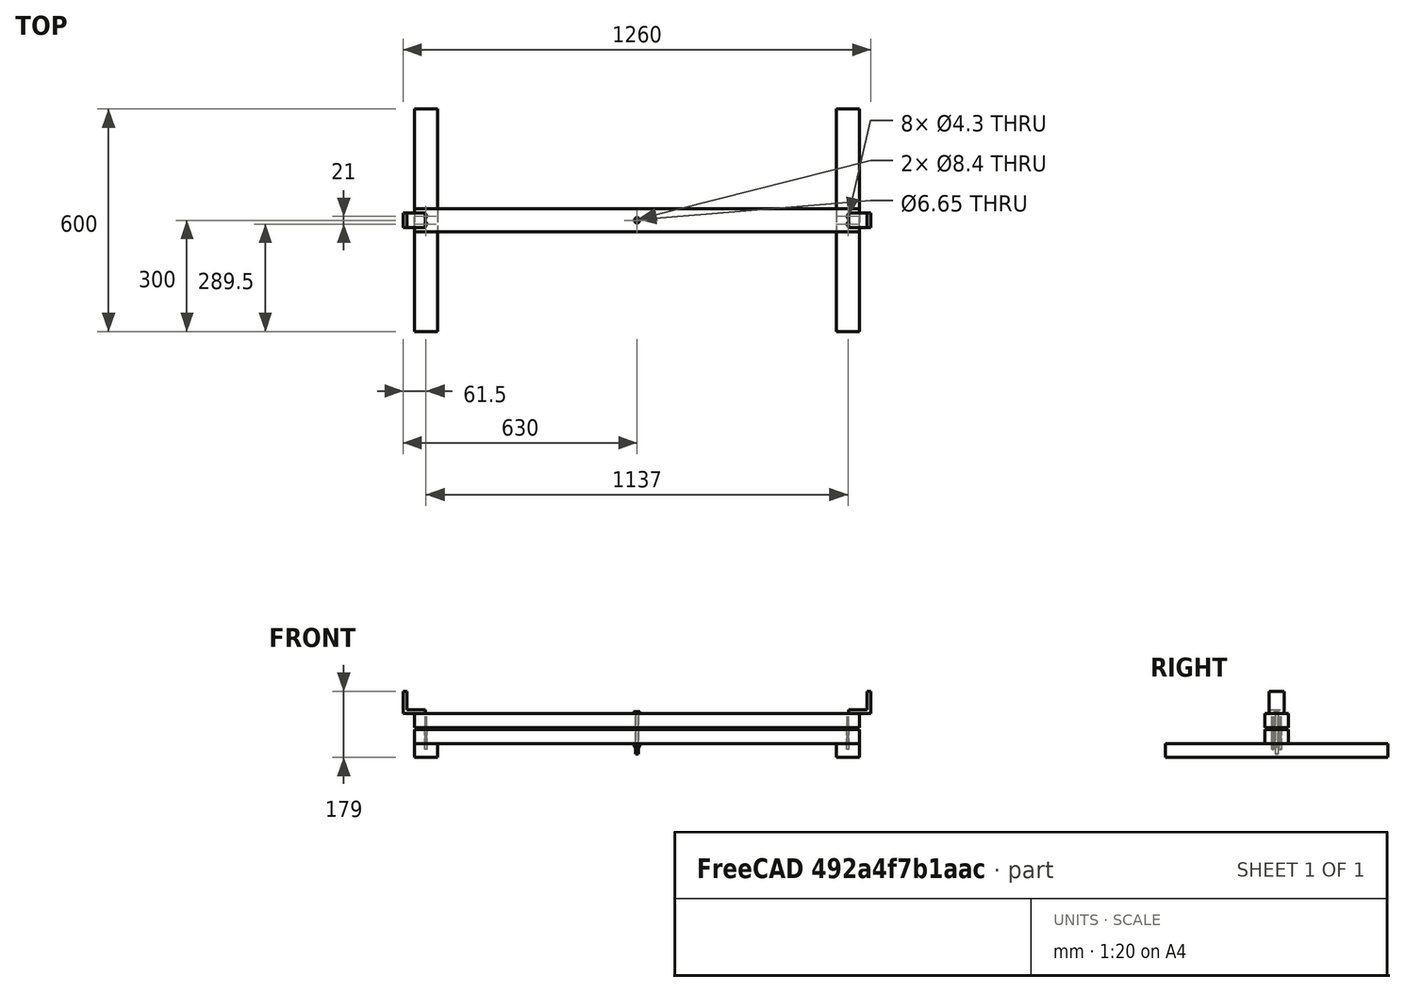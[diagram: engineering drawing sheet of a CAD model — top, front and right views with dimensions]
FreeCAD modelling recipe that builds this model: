
FCSTD DOCUMENT  (FreeCAD 0.21R33771 (Git))
Label: reflector_2024_base
License: All rights reserved
LicenseURL: http://en.wikipedia.org/wiki/All_rights_reserved
objects: Part::FeaturePython×12, Part::Compound×2, App::DocumentObjectGroupPython×1
note: 14 computed .brp shape members not serialized (recipe doc carries the construction recipe); baked Part::Feature solids carry a one-line shape summary decoded from their .brp

FEATURE [Part::FeaturePython] b_reflector_2024_timber_base_001_  label="reflector_2024_timber_base_001"  # a2plus imported part (geometry in sourceFile) (typed FeaturePython)
  Placement = pos=(0,0,0) rot=(1,0,0;1.5708rad)
  a2p_Version = 0.4.64
  fixedPosition = true
  objectType = a2pPart
  sourceFile = .\reflector_2024_timber_base.FCStd
  subassemblyImport = false
  timeLastImport = 1.71095e+09
  updateColors = true
FEATURE [Part::FeaturePython] b_reflector_2024_timber_half_001_  label="reflector_2024_timber_half_001"  # a2plus imported part (geometry in sourceFile) (typed FeaturePython)
  Placement = pos=(568.5,0,-38) rot=(0.57735,-0.57735,0.57735;4.18879rad)
  a2p_Version = 0.4.64
  fixedPosition = false
  objectType = a2pPart
  sourceFile = .\reflector_2024_timber_half.FCStd
  subassemblyImport = false
  timeLastImport = 1.71052e+09
  updateColors = true
  expr: .Placement.Base.x = 600 - 63 / 2
  expr: .Placement.Base.z = -38
FEATURE [Part::FeaturePython] b_reflector_2024_timber_half_001_001  label="reflector_2024_timber_half_002"  # a2plus imported part (geometry in sourceFile) (typed FeaturePython)
  Placement = pos=(-568.5,-9e-15,-38) rot=(0.57735,-0.57735,0.57735;4.18879rad)
  a2p_Version = 0.4.64
  fixedPosition = false
  objectType = a2pPart
  sourceFile = .\reflector_2024_timber_half.FCStd
  subassemblyImport = false
  timeLastImport = 1.71052e+09
  updateColors = true
  expr: .Placement.Base.x = -(600 - 63 / 2)
  expr: .Placement.Base.z = -38
FEATURE [Part::FeaturePython] b_L_corner_001_  label="L_corner_001"  # a2plus imported part (geometry in sourceFile) (typed FeaturePython)
  Placement = pos=(-630,0,62) rot=(0,0,1;3.14159rad)
  a2p_Version = 0.4.64
  fixedPosition = false
  objectType = a2pPart
  sourceFile = .\L_corner.FCStd
  subassemblyImport = false
  timeLastImport = 1.71093e+09
  updateColors = true
  expr: .Placement.Base.x = -600 - 30
  expr: .Placement.Base.z = 38 / 2 + 38 + 5
FEATURE [Part::FeaturePython] b_L_corner_001_001  label="L_corner_002"  # a2plus imported part (geometry in sourceFile) (typed FeaturePython)
  Placement = pos=(630,0,62) rot=(0,0,1;0rad)
  a2p_Version = 0.4.64
  fixedPosition = false
  objectType = a2pPart
  sourceFile = .\L_corner.FCStd
  subassemblyImport = false
  timeLastImport = 1.71093e+09
  updateColors = true
  expr: .Placement.Base.x = 600 + 30
  expr: .Placement.Base.z = 38 / 2 + 38 + 5
FEATURE [Part::FeaturePython] Screw  label="M6x55-Screw"  # Fasteners workbench fastener (typed FeaturePython)
  Placement = pos=(568.5,10.5,20) rot=(0,0,1;0rad)
  diameter = 8
  invert = false
  leftHanded = false
  length = 12
  lengthCustom = 55
  matchOuter = false
  offset = 0
  thread = false
  type = 73
FEATURE [Part::FeaturePython] Screw001  label="M6x55-Screw004"  # Fasteners workbench fastener (typed FeaturePython)
  Placement = pos=(568.5,-10.5,20) rot=(0,0,1;0rad)
  diameter = 8
  invert = false
  leftHanded = false
  length = 12
  lengthCustom = 55
  matchOuter = false
  offset = 0
  thread = false
  type = 73
FEATURE [Part::FeaturePython] Screw002  label="M6x55-Screw005"  # Fasteners workbench fastener (typed FeaturePython)
  Placement = pos=(-568.5,10.5,20) rot=(0,0,1;0rad)
  diameter = 8
  invert = false
  leftHanded = false
  length = 12
  lengthCustom = 55
  matchOuter = false
  offset = 0
  thread = false
  type = 73
FEATURE [Part::FeaturePython] Screw003  label="M6x55-Screw006"  # Fasteners workbench fastener (typed FeaturePython)
  Placement = pos=(-568.5,-10.5,20) rot=(0,0,1;0rad)
  diameter = 8
  invert = false
  leftHanded = false
  length = 12
  lengthCustom = 55
  matchOuter = false
  offset = 0
  thread = false
  type = 73
FEATURE [App::DocumentObjectGroupPython] ExplodedAssembly  # scripted group (container) (typed FeaturePython)
  AnimationStep = 0
  CurrentTrajectory = -1
  InAnimation = false
  RemoveAllTrajectories = false
  ResetAnimation = false
FEATURE [Part::FeaturePython] b_reflector_2024_timber_base_001_001  label="reflector_2024_timber_base_002"  # a2plus imported part (geometry in sourceFile) (typed FeaturePython)
  Placement = pos=(0,0,43) rot=(1,0,0;1.5708rad)
  a2p_Version = 0.4.64
  fixedPosition = false
  objectType = a2pPart
  sourceFile = .\reflector_2024_timber_base.FCStd
  subassemblyImport = false
  timeLastImport = 1.71095e+09
  updateColors = true
  expr: .Placement.Base.z = 38 + 5
FEATURE [Part::Compound] Compound  label="base_1"
  Links = -> [b_reflector_2024_timber_base_001_,b_reflector_2024_timber_half_001_,b_reflector_2024_timber_half_001_001]
FEATURE [Part::Compound] Compound001  label="base_2"
  Links = -> [b_L_corner_001_,b_L_corner_001_001,b_reflector_2024_timber_base_001_001]
FEATURE [Part::FeaturePython] Screw004  label="M8x110-Screw"  # Fasteners workbench fastener (typed FeaturePython)
  Placement = pos=(0,0,62) rot=(0,0,1;0rad)
  diameter = 9
  invert = false
  leftHanded = false
  length = 11
  lengthCustom = 110
  matchOuter = false
  offset = 0
  thread = false
  type = 60
FEATURE [Part::FeaturePython] Nut001  label="M8-Nut"  # Fasteners workbench fastener (typed FeaturePython)
  Placement = pos=(0,0,-19) rot=(0,1,0;3.14159rad)
  diameter = 3
  invert = false
  leftHanded = false
  matchOuter = false
  offset = 0
  thread = false
  type = 39
